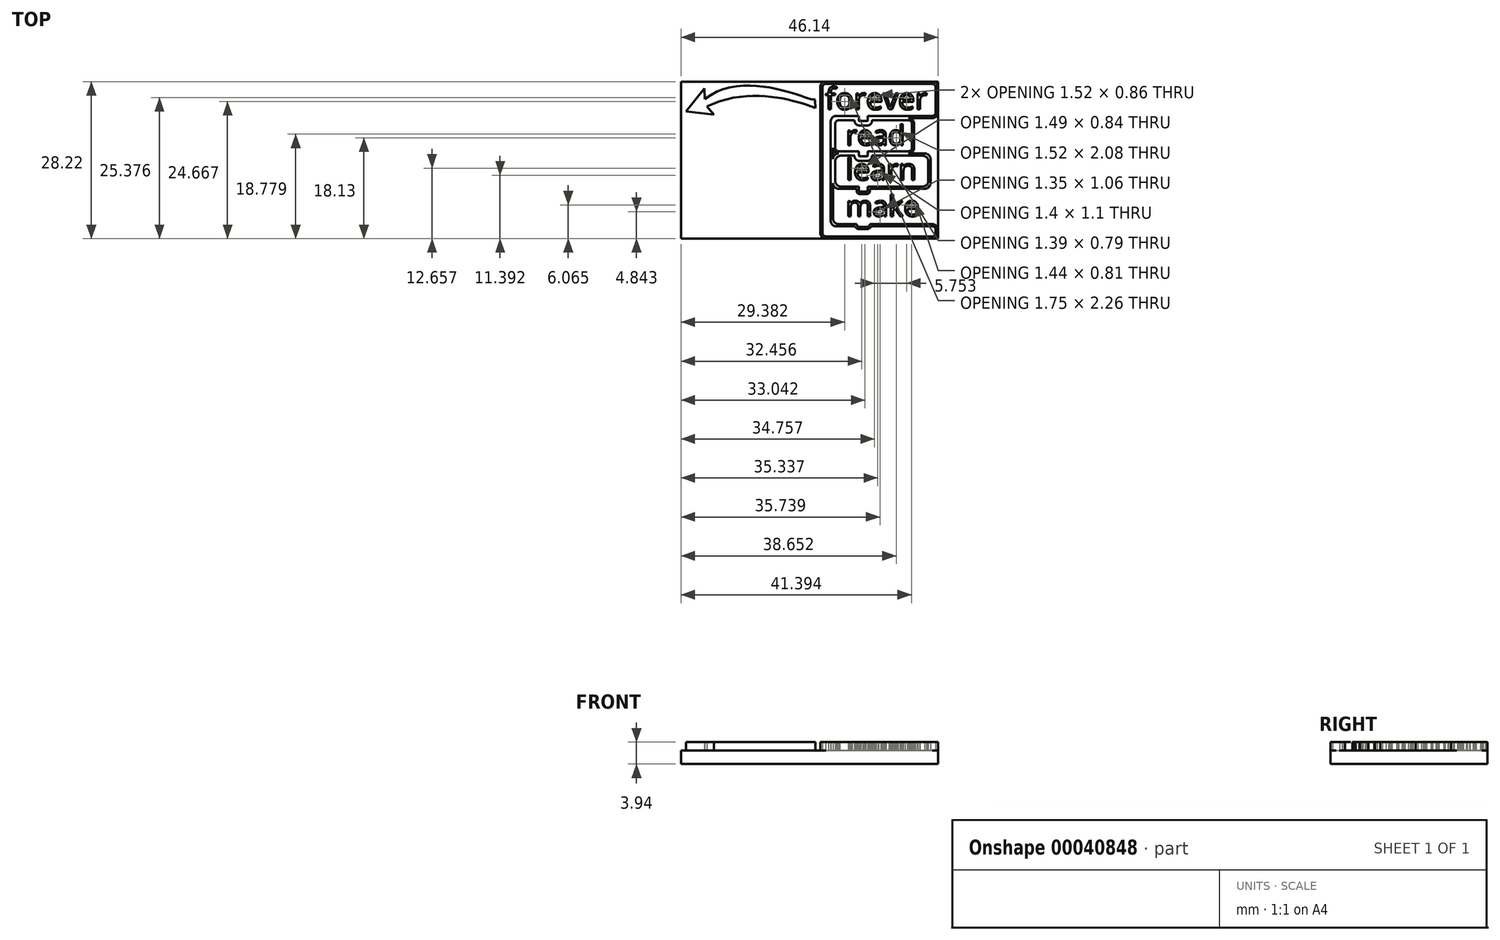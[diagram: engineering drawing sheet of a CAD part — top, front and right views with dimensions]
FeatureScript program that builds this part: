
annotation { "Feature Type Name" : "Feature", "Feature Type Description" : "" }
export const myFeature = defineFeature(function(context is Context, id is Id, definition is map)
    precondition{}
    {
        {
            var Q0;
            Q0=qCreatedBy(makeId("Top.planeOp"),FACE);
            var sketch = newSketch(context, id + "F0", { "sketchPlane" : qUnion([Q0])});
            skLineSegment(sketch, "E0", {"start": v(-1.02, 0) * mm, "end": v(-20.12, 0) * mm});
            skLineSegment(sketch, "E1", {"start": v(-21.14, -1.02) * mm, "end": v(-21.14, -27.2) * mm});
            skLineSegment(sketch, "E2", {"start": v(-20.12, -28.21) * mm, "end": v(-1.02, -28.21) * mm});
            skLineSegment(sketch, "E3", {"start": v(0, -27.2) * mm, "end": v(0, -26.62) * mm});
            skLineSegment(sketch, "E4", {"start": v(-1.02, -25.6) * mm, "end": v(-12.22, -25.6) * mm});
            skLineSegment(sketch, "E5", {"start": v(-18.86, -18.24) * mm, "end": v(-18.86, -7.57) * mm});
            skLineSegment(sketch, "E6", {"start": v(-17.84, -6.56) * mm, "end": v(-14.6, -6.56) * mm});
            skLineSegment(sketch, "E7", {"start": v(0, -5.54) * mm, "end": v(0, -1.02) * mm});
            skLineSegment(sketch, "E8.top", {"start": v(-17.84, -12.9) * mm, "end": v(-14.6, -12.9) * mm});
            skLineSegment(sketch, "E8.left", {"start": v(-18.86, -7.57) * mm, "end": v(-18.86, -11.9) * mm});
            skLineSegment(sketch, "E8.right", {"start": v(-4.27, -7.57) * mm, "end": v(-4.27, -11.9) * mm});
            skText(sketch, "E9", { "text": "read", "fontName": "OpenSans-Regular.ttf"});
            skLineSegment(sketch, "E10.top", {"start": v(-18.86, -19.26) * mm, "end": v(-14.6, -19.26) * mm});
            skLineSegment(sketch, "E10.left", {"start": v(-18.86, -13.92) * mm, "end": v(-18.86, -19.26) * mm});
            skLineSegment(sketch, "E10.right", {"start": v(-1.33, -13.92) * mm, "end": v(-1.33, -18.24) * mm});
            skText(sketch, "E11", { "text": "learn", "fontName": "OpenSans-Regular.ttf"});
            skText(sketch, "E12", { "text": "make", "fontName": "OpenSans-Regular.ttf"});
            skLineSegment(sketch, "E13.bottom", {"start": v(-17.84, -19.26) * mm, "end": v(-14.6, -19.26) * mm});
            skLineSegment(sketch, "E13.top", {"start": v(-17.86, -25.6) * mm, "end": v(-14.58, -25.6) * mm});
            skLineSegment(sketch, "E13.left", {"start": v(-18.86, -20.27) * mm, "end": v(-18.86, -24.6) * mm});
            skLineSegment(sketch, "E14", {"start": v(-14.6, -6.56) * mm, "end": v(-14.6, -6.99) * mm});
            skLineSegment(sketch, "E15", {"start": v(-14.08, -7.5) * mm, "end": v(-12.73, -7.5) * mm});
            skLineSegment(sketch, "E16", {"start": v(-12.23, -6.99) * mm, "end": v(-12.23, -6.56) * mm});
            skLineSegment(sketch, "E17", {"start": v(-14.6, -12.9) * mm, "end": v(-14.6, -13.34) * mm});
            skLineSegment(sketch, "E18", {"start": v(-14.6, -19.26) * mm, "end": v(-14.6, -19.69) * mm});
            skLineSegment(sketch, "E19", {"start": v(-14.08, -20.2) * mm, "end": v(-12.73, -20.2) * mm});
            skLineSegment(sketch, "E20", {"start": v(-12.23, -19.69) * mm, "end": v(-12.23, -19.26) * mm});
            skLineSegment(sketch, "E21", {"start": v(-14.08, -13.85) * mm, "end": v(-12.73, -13.85) * mm});
            skLineSegment(sketch, "E22", {"start": v(-12.23, -13.34) * mm, "end": v(-12.23, -12.9) * mm});
            skText(sketch, "E23", { "text": "forever", "fontName": "OpenSans-Regular.ttf"});
            skPoint(sketch, "E24.visualSharp", {"position": v(-21.14, 0) * mm});
            skArc(sketch, "E24.filletArc", {"start": v(-20.12, 0) * mm, "mid": v(-20.84, -0.3) * mm, "end": v(-21.14, -1.02) * mm});
            skPoint(sketch, "E25.visualSharp", {"position": v(0, 0) * mm});
            skArc(sketch, "E25.filletArc", {"start": v(0, -1.02) * mm, "mid": v(-0.3, -0.3) * mm, "end": v(-1.02, 0) * mm});
            skPoint(sketch, "E26.visualSharp", {"position": v(0, -6.56) * mm});
            skArc(sketch, "E26.filletArc", {"start": v(-1.02, -6.56) * mm, "mid": v(-0.3, -6.26) * mm, "end": v(0, -5.54) * mm});
            skPoint(sketch, "E27.visualSharp", {"position": v(-1.33, -12.9) * mm});
            skArc(sketch, "E27.filletArc", {"start": v(-1.33, -13.92) * mm, "mid": v(-1.63, -13.2) * mm, "end": v(-2.34, -12.9) * mm});
            skPoint(sketch, "E28.visualSharp", {"position": v(-1.33, -19.26) * mm});
            skArc(sketch, "E28.filletArc", {"start": v(-2.34, -19.26) * mm, "mid": v(-1.63, -18.96) * mm, "end": v(-1.33, -18.24) * mm});
            skPoint(sketch, "E29.visualSharp", {"position": v(0, -25.6) * mm});
            skArc(sketch, "E29.filletArc", {"start": v(0, -26.62) * mm, "mid": v(-0.3, -25.9) * mm, "end": v(-1.02, -25.6) * mm});
            skPoint(sketch, "E30.visualSharp", {"position": v(-21.14, -28.21) * mm});
            skArc(sketch, "E30.filletArc", {"start": v(-21.14, -27.2) * mm, "mid": v(-20.84, -27.92) * mm, "end": v(-20.12, -28.21) * mm});
            skPoint(sketch, "E31.visualSharp", {"position": v(-18.86, -25.6) * mm});
            skArc(sketch, "E31.filletArc", {"start": v(-18.86, -24.6) * mm, "mid": v(-18.56, -25.3) * mm, "end": v(-17.84, -25.6) * mm});
            skPoint(sketch, "E32.visualSharp", {"position": v(-18.86, -6.56) * mm});
            skArc(sketch, "E32.filletArc", {"start": v(-17.84, -6.56) * mm, "mid": v(-18.56, -6.85) * mm, "end": v(-18.86, -7.57) * mm});
            skPoint(sketch, "E33.visualSharp", {"position": v(0, -28.21) * mm});
            skArc(sketch, "E33.filletArc", {"start": v(-1.02, -28.21) * mm, "mid": v(-0.3, -27.92) * mm, "end": v(0, -27.2) * mm});
            skPoint(sketch, "E34.visualSharp", {"position": v(-4.27, -6.56) * mm});
            skArc(sketch, "E34.filletArc", {"start": v(-4.27, -7.57) * mm, "mid": v(-4.57, -6.85) * mm, "end": v(-5.28, -6.56) * mm});
            skPoint(sketch, "E35.visualSharp", {"position": v(-4.27, -12.9) * mm});
            skArc(sketch, "E35.filletArc", {"start": v(-5.28, -12.9) * mm, "mid": v(-4.57, -12.6) * mm, "end": v(-4.27, -11.9) * mm});
            skPoint(sketch, "E36.visualSharp", {"position": v(-3.03, -19.26) * mm});
            skPoint(sketch, "E37.visualSharp", {"position": v(-14.6, -7.5) * mm});
            skArc(sketch, "E37.filletArc", {"start": v(-14.6, -6.99) * mm, "mid": v(-14.44, -7.35) * mm, "end": v(-14.08, -7.5) * mm});
            skPoint(sketch, "E38.visualSharp", {"position": v(-12.23, -7.5) * mm});
            skArc(sketch, "E38.filletArc", {"start": v(-12.73, -7.5) * mm, "mid": v(-12.38, -7.35) * mm, "end": v(-12.23, -6.99) * mm});
            skPoint(sketch, "E39.visualSharp", {"position": v(-14.6, -13.85) * mm});
            skArc(sketch, "E39.filletArc", {"start": v(-14.6, -13.34) * mm, "mid": v(-14.44, -13.7) * mm, "end": v(-14.08, -13.85) * mm});
            skPoint(sketch, "E40.visualSharp", {"position": v(-12.23, -13.85) * mm});
            skArc(sketch, "E40.filletArc", {"start": v(-12.73, -13.85) * mm, "mid": v(-12.38, -13.7) * mm, "end": v(-12.23, -13.34) * mm});
            skPoint(sketch, "E41.visualSharp", {"position": v(-14.6, -20.2) * mm});
            skArc(sketch, "E41.filletArc", {"start": v(-14.6, -19.69) * mm, "mid": v(-14.44, -20.05) * mm, "end": v(-14.08, -20.2) * mm});
            skPoint(sketch, "E42.visualSharp", {"position": v(-12.23, -20.2) * mm});
            skArc(sketch, "E42.filletArc", {"start": v(-12.73, -20.2) * mm, "mid": v(-12.38, -20.05) * mm, "end": v(-12.23, -19.69) * mm});
            skLineSegment(sketch, "E43.trimOffspring", {"start": v(-12.23, -19.26) * mm, "end": v(-4.05, -19.26) * mm});
            skLineSegment(sketch, "E44.trimOffspring", {"start": v(-12.23, -12.9) * mm, "end": v(-5.28, -12.9) * mm});
            skLineSegment(sketch, "E45.trimOffspring", {"start": v(-12.23, -12.9) * mm, "end": v(-2.34, -12.9) * mm});
            skLineSegment(sketch, "E46.trimOffspring", {"start": v(-12.23, -19.26) * mm, "end": v(-2.34, -19.26) * mm});
            skLineSegment(sketch, "E47.trimOffspring", {"start": v(-12.23, -6.56) * mm, "end": v(-5.28, -6.56) * mm});
            skLineSegment(sketch, "E48.trimOffspring", {"start": v(-12.23, -6.56) * mm, "end": v(-1.02, -6.56) * mm});
            skPoint(sketch, "E49.visualSharp", {"position": v(-18.86, -12.9) * mm});
            skArc(sketch, "E49.filletArc", {"start": v(-18.86, -11.9) * mm, "mid": v(-18.56, -12.6) * mm, "end": v(-17.84, -12.9) * mm});
            skArc(sketch, "E50.filletArc", {"start": v(-18.86, -18.24) * mm, "mid": v(-18.56, -18.96) * mm, "end": v(-17.84, -19.26) * mm});
            skArc(sketch, "E51.filletArc", {"start": v(-17.84, -19.26) * mm, "mid": v(-18.56, -19.55) * mm, "end": v(-18.86, -20.27) * mm});
            skLineSegment(sketch, "E52", {"start": v(-5.28, -6.56) * mm, "end": v(-12.23, -6.56) * mm});
            skLineSegment(sketch, "E53", {"start": v(-4.05, -19.26) * mm, "end": v(-12.23, -19.26) * mm});
            skLineSegment(sketch, "E54.0", {"start": v(-17.84, -12.5) * mm, "end": v(-14.6, -12.5) * mm});
            skLineSegment(sketch, "E54.1", {"start": v(-17.84, -6.96) * mm, "end": v(-15, -6.96) * mm});
            skArc(sketch, "E54.2", {"start": v(-17.84, -6.96) * mm, "mid": v(-18.28, -7.14) * mm, "end": v(-18.46, -7.57) * mm});
            skLineSegment(sketch, "E54.3", {"start": v(-18.46, -7.57) * mm, "end": v(-18.46, -11.9) * mm});
            skArc(sketch, "E54.4", {"start": v(-18.46, -11.9) * mm, "mid": v(-18.28, -12.33) * mm, "end": v(-17.84, -12.5) * mm});
            skLineSegment(sketch, "E55.0", {"start": v(-5.28, -6.96) * mm, "end": v(-11.83, -6.96) * mm});
            skArc(sketch, "E55.1", {"start": v(-4.67, -7.57) * mm, "mid": v(-4.85, -7.14) * mm, "end": v(-5.28, -6.96) * mm});
            skLineSegment(sketch, "E55.2", {"start": v(-4.67, -7.57) * mm, "end": v(-4.67, -11.9) * mm});
            skArc(sketch, "E55.3", {"start": v(-5.28, -12.5) * mm, "mid": v(-4.85, -12.33) * mm, "end": v(-4.67, -11.9) * mm});
            skLineSegment(sketch, "E56.1", {"start": v(-12.63, -13.28) * mm, "end": v(-12.63, -12.5) * mm});
            skLineSegment(sketch, "E56.2", {"start": v(-14.02, -13.45) * mm, "end": v(-12.8, -13.45) * mm});
            skLineSegment(sketch, "E56.3", {"start": v(-14.2, -12.9) * mm, "end": v(-14.2, -13.28) * mm});
            skLineSegment(sketch, "E57", {"start": v(-14.6, -12.5) * mm, "end": v(-14.2, -12.5) * mm});
            skLineSegment(sketch, "E58", {"start": v(-14.2, -12.5) * mm, "end": v(-14.2, -12.9) * mm});
            skPoint(sketch, "E59.visualSharp", {"position": v(-14.2, -13.45) * mm});
            skArc(sketch, "E59.filletArc", {"start": v(-14.2, -13.28) * mm, "mid": v(-14.14, -13.4) * mm, "end": v(-14.02, -13.45) * mm});
            skPoint(sketch, "E60.visualSharp", {"position": v(-12.63, -13.45) * mm});
            skArc(sketch, "E60.filletArc", {"start": v(-12.8, -13.45) * mm, "mid": v(-12.68, -13.4) * mm, "end": v(-12.63, -13.28) * mm});
            skArc(sketch, "E61.0", {"start": v(-12.73, -7.9) * mm, "mid": v(-12.1, -7.63) * mm, "end": v(-11.83, -6.99) * mm});
            skLineSegment(sketch, "E61.1", {"start": v(-14.08, -7.9) * mm, "end": v(-12.73, -7.9) * mm});
            skArc(sketch, "E61.2", {"start": v(-15, -6.99) * mm, "mid": v(-14.72, -7.63) * mm, "end": v(-14.08, -7.9) * mm});
            skLineSegment(sketch, "E62", {"start": v(-15, -6.99) * mm, "end": v(-15, -6.96) * mm});
            skLineSegment(sketch, "E63", {"start": v(-11.83, -7) * mm, "end": v(-11.83, -6.96) * mm});
            skLineSegment(sketch, "E64.0", {"start": v(-1.02, -0.4) * mm, "end": v(-20.12, -0.4) * mm});
            skLineSegment(sketch, "E64.1", {"start": v(-12.23, -6.16) * mm, "end": v(-1.02, -6.16) * mm});
            skArc(sketch, "E64.2", {"start": v(-1.02, -6.16) * mm, "mid": v(-0.58, -5.98) * mm, "end": v(-0.4, -5.54) * mm});
            skLineSegment(sketch, "E64.3", {"start": v(-0.4, -5.54) * mm, "end": v(-0.4, -1.02) * mm});
            skArc(sketch, "E64.4", {"start": v(-0.4, -1.02) * mm, "mid": v(-0.58, -0.58) * mm, "end": v(-1.02, -0.4) * mm});
            skArc(sketch, "E65.1", {"start": v(-0.4, -26.62) * mm, "mid": v(-0.58, -26.19) * mm, "end": v(-1.02, -26) * mm});
            skLineSegment(sketch, "E65.2", {"start": v(-0.4, -27.2) * mm, "end": v(-0.4, -26.62) * mm});
            skArc(sketch, "E65.3", {"start": v(-1.02, -27.81) * mm, "mid": v(-0.58, -27.63) * mm, "end": v(-0.4, -27.2) * mm});
            skArc(sketch, "E65.4", {"start": v(-20.12, -0.4) * mm, "mid": v(-20.56, -0.58) * mm, "end": v(-20.74, -1.02) * mm});
            skLineSegment(sketch, "E65.5", {"start": v(-20.74, -1.02) * mm, "end": v(-20.74, -27.2) * mm});
            skArc(sketch, "E65.6", {"start": v(-20.74, -27.2) * mm, "mid": v(-20.56, -27.63) * mm, "end": v(-20.12, -27.81) * mm});
            skLineSegment(sketch, "E65.7", {"start": v(-20.12, -27.81) * mm, "end": v(-1.02, -27.81) * mm});
            skLineSegment(sketch, "E66", {"start": v(-18.86, -20.27) * mm, "end": v(-18.86, -19.26) * mm});
            skLineSegment(sketch, "E67", {"start": v(-19.26, -24.6) * mm, "end": v(-19.26, -7.17) * mm});
            skLineSegment(sketch, "E68", {"start": v(-12.23, -6.16) * mm, "end": v(-12.63, -6.16) * mm});
            skPoint(sketch, "E69.visualSharp", {"position": v(-19.26, -6.16) * mm});
            skArc(sketch, "E69.filletArc", {"start": v(-18.24, -6.16) * mm, "mid": v(-18.96, -6.45) * mm, "end": v(-19.26, -7.17) * mm});
            skLineSegment(sketch, "E70", {"start": v(-17.84, -26) * mm, "end": v(-18.24, -26) * mm});
            skLineSegment(sketch, "E71", {"start": v(-19.26, -24.6) * mm, "end": v(-19.26, -25) * mm});
            skPoint(sketch, "E72.visualSharp", {"position": v(-19.26, -26) * mm});
            skArc(sketch, "E72.filletArc", {"start": v(-19.26, -25) * mm, "mid": v(-18.96, -25.7) * mm, "end": v(-18.24, -26) * mm});
            skArc(sketch, "E73.filletArc", {"start": v(-18.86, -24.6) * mm, "mid": v(-18.56, -25.31) * mm, "end": v(-17.86, -25.6) * mm});
            skLineSegment(sketch, "E74", {"start": v(-17.84, -12.9) * mm, "end": v(-17.84, -12.9) * mm});
            skArc(sketch, "E75.filletArc", {"start": v(-17.84, -12.9) * mm, "mid": v(-18.56, -13.2) * mm, "end": v(-18.86, -13.92) * mm});
            skLineSegment(sketch, "E76", {"start": v(-18.86, -13.92) * mm, "end": v(-18.86, -18.24) * mm});
            skLineSegment(sketch, "E77", {"start": v(-18.46, -14.75) * mm, "end": v(-18.46, -17.84) * mm});
            skLineSegment(sketch, "E78", {"start": v(-18.46, -14.75) * mm, "end": v(-18.46, -14.32) * mm});
            skPoint(sketch, "E79.orphan", {"position": v(-17.84, -13.3) * mm});
            skLineSegment(sketch, "E80", {"start": v(-1.73, -15.83) * mm, "end": v(-1.73, -14.32) * mm});
            skLineSegment(sketch, "E81", {"start": v(-1.73, -15.83) * mm, "end": v(-1.73, -17.84) * mm});
            skLineSegment(sketch, "E82", {"start": v(-12.23, -18.86) * mm, "end": v(-2.74, -18.86) * mm});
            skLineSegment(sketch, "E83", {"start": v(-12.23, -18.86) * mm, "end": v(-12.63, -18.86) * mm});
            skLineSegment(sketch, "E84.0", {"start": v(-12.63, -19.69) * mm, "end": v(-12.63, -19.26) * mm});
            skLineSegment(sketch, "E84.1", {"start": v(-14.2, -19.26) * mm, "end": v(-14.2, -19.69) * mm});
            skArc(sketch, "E84.2", {"start": v(-14.2, -19.69) * mm, "mid": v(-14.16, -19.77) * mm, "end": v(-14.08, -19.8) * mm});
            skLineSegment(sketch, "E84.3", {"start": v(-14.08, -19.8) * mm, "end": v(-12.73, -19.8) * mm});
            skArc(sketch, "E84.4", {"start": v(-12.73, -19.8) * mm, "mid": v(-12.66, -19.77) * mm, "end": v(-12.63, -19.69) * mm});
            skLineSegment(sketch, "E85", {"start": v(-14.2, -19.26) * mm, "end": v(-14.2, -18.86) * mm});
            skLineSegment(sketch, "E86", {"start": v(-12.63, -19.26) * mm, "end": v(-12.63, -18.86) * mm});
            skLineSegment(sketch, "E87.trimOffspring", {"start": v(-14.2, -18.86) * mm, "end": v(-17.44, -18.86) * mm});
            skPoint(sketch, "E88.start.orphan", {"position": v(-18.86, -16.08) * mm});
            skLineSegment(sketch, "E89", {"start": v(-2.74, -13.3) * mm, "end": v(-11.83, -13.3) * mm});
            skPoint(sketch, "E90.visualSharp", {"position": v(-1.73, -13.3) * mm});
            skArc(sketch, "E90.filletArc", {"start": v(-1.73, -14.32) * mm, "mid": v(-2.03, -13.6) * mm, "end": v(-2.74, -13.3) * mm});
            skPoint(sketch, "E91.visualSharp", {"position": v(-1.73, -18.86) * mm});
            skArc(sketch, "E91.filletArc", {"start": v(-2.74, -18.86) * mm, "mid": v(-2.03, -18.56) * mm, "end": v(-1.73, -17.84) * mm});
            skPoint(sketch, "E92.visualSharp", {"position": v(-18.46, -18.86) * mm});
            skArc(sketch, "E92.filletArc", {"start": v(-18.46, -17.84) * mm, "mid": v(-18.16, -18.56) * mm, "end": v(-17.44, -18.86) * mm});
            skPoint(sketch, "E93.visualSharp", {"position": v(-18.46, -13.3) * mm});
            skArc(sketch, "E93.filletArc", {"start": v(-17.44, -13.3) * mm, "mid": v(-18.16, -13.6) * mm, "end": v(-18.46, -14.32) * mm});
            skLineSegment(sketch, "E94", {"start": v(-18.46, -22.2) * mm, "end": v(-18.46, -20.13) * mm});
            skLineSegment(sketch, "E95", {"start": v(-18.46, -22.2) * mm, "end": v(-18.46, -24.82) * mm});
            skLineSegment(sketch, "E96", {"start": v(-17.84, -19.66) * mm, "end": v(-17.84, -19.66) * mm});
            skPoint(sketch, "E97.endSnap0", {"position": v(-18.56, -25.31) * mm});
            skLineSegment(sketch, "E98", {"start": v(-2.63, -22.43) * mm, "end": v(-2.63, -24.6) * mm});
            skLineSegment(sketch, "E99", {"start": v(-2.63, -22.43) * mm, "end": v(-2.63, -20.27) * mm});
            skLineSegment(sketch, "E100", {"start": v(-17.84, -19.66) * mm, "end": v(-18, -19.66) * mm});
            skLineSegment(sketch, "E101", {"start": v(-17.84, -19.66) * mm, "end": v(-15, -19.66) * mm});
            skLineSegment(sketch, "E102", {"start": v(-3.65, -25.6) * mm, "end": v(-4.05, -25.6) * mm});
            skLineSegment(sketch, "E103", {"start": v(-4.05, -19.26) * mm, "end": v(-3.65, -19.26) * mm});
            skLineSegment(sketch, "E104", {"start": v(-11.83, -19.69) * mm, "end": v(-4.05, -19.69) * mm});
            skArc(sketch, "E105.0", {"start": v(-12.73, -20.6) * mm, "mid": v(-12.1, -20.33) * mm, "end": v(-11.83, -19.69) * mm});
            skLineSegment(sketch, "E105.1", {"start": v(-14.08, -20.6) * mm, "end": v(-12.73, -20.6) * mm});
            skArc(sketch, "E105.2", {"start": v(-15, -19.66) * mm, "mid": v(-14.74, -20.32) * mm, "end": v(-14.08, -20.6) * mm});
            skPoint(sketch, "E106.orphan", {"position": v(-11.94, -19.69) * mm});
            skLineSegment(sketch, "E107", {"start": v(-18.07, -25.19) * mm, "end": v(-14.18, -25.19) * mm});
            skLineSegment(sketch, "E108", {"start": v(-12.63, -6.16) * mm, "end": v(-12.63, -7.03) * mm});
            skLineSegment(sketch, "E109", {"start": v(-14.2, -6.16) * mm, "end": v(-14.2, -7.03) * mm});
            skLineSegment(sketch, "E110", {"start": v(-14.08, -7.1) * mm, "end": v(-14.13, -7.1) * mm});
            skLineSegment(sketch, "E111", {"start": v(-14.08, -7.1) * mm, "end": v(-12.69, -7.1) * mm});
            skPoint(sketch, "E112.visualSharp", {"position": v(-14.2, -7.1) * mm});
            skArc(sketch, "E112.filletArc", {"start": v(-14.2, -7.03) * mm, "mid": v(-14.17, -7.08) * mm, "end": v(-14.13, -7.1) * mm});
            skPoint(sketch, "E113.visualSharp", {"position": v(-12.63, -7.1) * mm});
            skArc(sketch, "E113.filletArc", {"start": v(-12.69, -7.1) * mm, "mid": v(-12.64, -7.08) * mm, "end": v(-12.63, -7.03) * mm});
            skLineSegment(sketch, "E114.trimOffspring", {"start": v(-14.2, -6.16) * mm, "end": v(-18.24, -6.16) * mm});
            skArc(sketch, "E115.0", {"start": v(-12.73, -14.25) * mm, "mid": v(-12.08, -13.97) * mm, "end": v(-11.83, -13.3) * mm});
            skLineSegment(sketch, "E115.1", {"start": v(-14.08, -14.25) * mm, "end": v(-12.73, -14.25) * mm});
            skArc(sketch, "E115.2", {"start": v(-15, -13.3) * mm, "mid": v(-14.74, -13.97) * mm, "end": v(-14.08, -14.25) * mm});
            skLineSegment(sketch, "E116.trimOffspring", {"start": v(-15, -13.3) * mm, "end": v(-17.44, -13.3) * mm});
            skLineSegment(sketch, "E117", {"start": v(-5.28, -12.5) * mm, "end": v(-12.63, -12.5) * mm});
            skPoint(sketch, "E118.visualSharp", {"position": v(-2.63, -19.26) * mm});
            skArc(sketch, "E118.filletArc", {"start": v(-2.63, -20.27) * mm, "mid": v(-2.93, -19.55) * mm, "end": v(-3.65, -19.26) * mm});
            skPoint(sketch, "E119.visualSharp", {"position": v(-3.03, -25.19) * mm});
            skArc(sketch, "E119.filletArc", {"start": v(-4.05, -25.19) * mm, "mid": v(-3.33, -24.9) * mm, "end": v(-3.03, -24.17) * mm});
            skPoint(sketch, "E120.visualSharp", {"position": v(-3.03, -19.69) * mm});
            skPoint(sketch, "E121.visualSharp", {"position": v(-2.63, -25.6) * mm});
            skArc(sketch, "E121.filletArc", {"start": v(-3.65, -25.6) * mm, "mid": v(-2.93, -25.3) * mm, "end": v(-2.63, -24.6) * mm});
            skLineSegment(sketch, "E122", {"start": v(-3.03, -24.17) * mm, "end": v(-3.03, -20.7) * mm});
            skArc(sketch, "E123.filletArc", {"start": v(-3.03, -20.7) * mm, "mid": v(-3.33, -19.99) * mm, "end": v(-4.05, -19.69) * mm});
            skArc(sketch, "E124.filletArc", {"start": v(-12.73, -26.12) * mm, "mid": v(-12.37, -25.97) * mm, "end": v(-12.22, -25.61) * mm});
            skLineSegment(sketch, "E125", {"start": v(-14.58, -25.18) * mm, "end": v(-14.58, -25.19) * mm});
            skPoint(sketch, "E126.orphan", {"position": v(-11.93, -25.61) * mm});
            skLineSegment(sketch, "E127", {"start": v(-14.08, -26.12) * mm, "end": v(-12.73, -26.12) * mm});
            skPoint(sketch, "E124.visualSharp", {"position": v(-12.22, -26.12) * mm});
            skArc(sketch, "E128.filletArc", {"start": v(-14.58, -25.61) * mm, "mid": v(-14.43, -25.97) * mm, "end": v(-14.08, -26.12) * mm});
            skLineSegment(sketch, "E129.3", {"start": v(-14.08, -25.72) * mm, "end": v(-12.73, -25.72) * mm});
            skPoint(sketch, "E128.visualSharp", {"position": v(-14.58, -26.12) * mm});
            skArc(sketch, "E129.4", {"start": v(-12.73, -25.72) * mm, "mid": v(-12.65, -25.69) * mm, "end": v(-12.62, -25.61) * mm});
            skArc(sketch, "E129.2", {"start": v(-14.18, -25.61) * mm, "mid": v(-14.15, -25.69) * mm, "end": v(-14.08, -25.72) * mm});
            skLineSegment(sketch, "E130", {"start": v(-14.18, -25.61) * mm, "end": v(-14.18, -25.19) * mm});
            skLineSegment(sketch, "E131", {"start": v(-12.62, -25.19) * mm, "end": v(-12.62, -25.61) * mm});
            skLineSegment(sketch, "E132", {"start": v(-12.22, -25.61) * mm, "end": v(-12.22, -25.6) * mm});
            skLineSegment(sketch, "E133.trimOffspring", {"start": v(-12.62, -25.19) * mm, "end": v(-4.05, -25.19) * mm});
            skLineSegment(sketch, "E134.trimOffspring", {"start": v(-14.58, -25.6) * mm, "end": v(-17.84, -25.6) * mm});
            skLineSegment(sketch, "E135.trimOffspring", {"start": v(-11.82, -25.6) * mm, "end": v(-4.05, -25.6) * mm});
            skLineSegment(sketch, "E136.trimOffspring", {"start": v(-14.58, -25.6) * mm, "end": v(-14.58, -25.61) * mm});
            skLineSegment(sketch, "E137", {"start": v(-14.58, -25.6) * mm, "end": v(-14.98, -25.6) * mm});
            skLineSegment(sketch, "E138", {"start": v(-12.22, -25.6) * mm, "end": v(-11.82, -25.6) * mm});
            skLineSegment(sketch, "E139", {"start": v(-11.82, -25.5) * mm, "end": v(-11.82, -25.6) * mm});
            skPoint(sketch, "E140.visualSharp", {"position": v(-11.82, -26.52) * mm});
            skArc(sketch, "E140.filletArc", {"start": v(-12.84, -26.52) * mm, "mid": v(-12.32, -26.38) * mm, "end": v(-11.95, -26) * mm});
            skArc(sketch, "E141", {"start": v(-14.9, -26) * mm, "mid": v(-14.6, -26.36) * mm, "end": v(-14.17, -26.52) * mm});
            skLineSegment(sketch, "E142", {"start": v(-14.17, -26.52) * mm, "end": v(-12.84, -26.52) * mm});
            skLineSegment(sketch, "E143.trimOffspring", {"start": v(-14.9, -26) * mm, "end": v(-17.84, -26) * mm});
            skLineSegment(sketch, "E144", {"start": v(-1.02, -26) * mm, "end": v(-11.95, -26) * mm});
            skArc(sketch, "E145.trimOffspring", {"start": v(-11.82, -25.6) * mm, "mid": v(-11.82, -25.56) * mm, "end": v(-11.82, -25.5) * mm});
            skPoint(sketch, "E146.visualSharp", {"position": v(-18.46, -25.19) * mm});
            skArc(sketch, "E147", {"start": v(-18.46, -24.76) * mm, "mid": v(-18.36, -25.06) * mm, "end": v(-18.07, -25.19) * mm});
            skArc(sketch, "E148", {"start": v(-18, -19.66) * mm, "mid": v(-18.32, -19.8) * mm, "end": v(-18.46, -20.13) * mm});
            const initialGuessF0  = {"E9": [-0.01653, -0.01142, 1, 0, 0.00358], "E11": [-0.01653, -0.01768, 1, 0, 0.00383], "E12": [-0.01653, -0.0242, 1, 0, 0.0037], "E23": [-0.02023, -0.005, 1, 0, 0.0039]};
            skSetInitialGuess(sketch, initialGuessF0);
            skSolve(sketch);
        }
        {
            var Q0;
            Q0=makeQuery(id+"F0.imprint","IMPRINT",FACE,{"disambiguationData":[TD([[makeQuery(id+"F0.imprint","IMPRINT",EDGE,{"derivedFrom":sQuery(id+"F0.wireOp",EDGE,"E23.sketch_text.stroke-0")}),-1.0]])]});
            var Q1;
            Q1=makeQuery(id+"F0.imprint","IMPRINT",FACE,{"disambiguationData":[TD([[makeQuery(id+"F0.imprint","IMPRINT",EDGE,{"derivedFrom":sQuery(id+"F0.wireOp",EDGE,"E23.sketch_text.stroke-17")}),-1.0]])]});
            var Q2;
            Q2=makeQuery(id+"F0.imprint","IMPRINT",FACE,{"disambiguationData":[TD([[makeQuery(id+"F0.imprint","IMPRINT",EDGE,{"derivedFrom":sQuery(id+"F0.wireOp",EDGE,"E23.sketch_text.stroke-34")}),-1.0]])]});
            var Q3;
            Q3=makeQuery(id+"F0.imprint","IMPRINT",FACE,{"disambiguationData":[TD([[makeQuery(id+"F0.imprint","IMPRINT",EDGE,{"derivedFrom":sQuery(id+"F0.wireOp",EDGE,"E23.sketch_text.stroke-47")}),-1.0]])]});
            var Q4;
            Q4=makeQuery(id+"F0.imprint","IMPRINT",FACE,{"disambiguationData":[TD([[makeQuery(id+"F0.imprint","IMPRINT",EDGE,{"derivedFrom":sQuery(id+"F0.wireOp",EDGE,"E23.sketch_text.stroke-66")}),-1.0]])]});
            var Q5;
            Q5=makeQuery(id+"F0.imprint","IMPRINT",FACE,{"disambiguationData":[TD([[makeQuery(id+"F0.imprint","IMPRINT",EDGE,{"derivedFrom":sQuery(id+"F0.wireOp",EDGE,"E23.sketch_text.stroke-76")}),-1.0]])]});
            var Q6;
            Q6=makeQuery(id+"F0.imprint","IMPRINT",FACE,{"disambiguationData":[TD([[makeQuery(id+"F0.imprint","IMPRINT",EDGE,{"derivedFrom":sQuery(id+"F0.wireOp",EDGE,"E23.sketch_text.stroke-95")}),-1.0]])]});
            var Q7;
            Q7=makeQuery(id+"F0.imprint","IMPRINT",FACE,{"disambiguationData":[TD([[makeQuery(id+"F0.imprint","IMPRINT",EDGE,{"derivedFrom":sQuery(id+"F0.wireOp",EDGE,"E9.sketch_text.stroke-0")}),-1.0]])]});
            var Q8;
            Q8=makeQuery(id+"F0.imprint","IMPRINT",FACE,{"disambiguationData":[TD([[makeQuery(id+"F0.imprint","IMPRINT",EDGE,{"derivedFrom":sQuery(id+"F0.wireOp",EDGE,"E9.sketch_text.stroke-13")}),-1.0]])]});
            var Q9;
            Q9=makeQuery(id+"F0.imprint","IMPRINT",FACE,{"disambiguationData":[TD([[makeQuery(id+"F0.imprint","IMPRINT",EDGE,{"derivedFrom":sQuery(id+"F0.wireOp",EDGE,"E9.sketch_text.stroke-32")}),-1.0]])]});
            var Q10;
            Q10=makeQuery(id+"F0.imprint","IMPRINT",FACE,{"disambiguationData":[TD([[makeQuery(id+"F0.imprint","IMPRINT",EDGE,{"derivedFrom":sQuery(id+"F0.wireOp",EDGE,"E11.sketch_text.stroke-0")}),-1.0]])]});
            extrude(context, id + "F1", {"entities" : qUnion([Q0, Q1, Q2, Q3, Q4, Q5, Q6, Q7, Q8, Q9, Q10]), "depth" : 1.5 * mm});
        }
        {
            var Q0;
            Q0=makeQuery(id+"F0.imprint","IMPRINT",FACE,{"disambiguationData":[TD([[makeQuery(id+"F0.imprint","IMPRINT",EDGE,{"derivedFrom":sQuery(id+"F0.wireOp",EDGE,"E12.sketch_text.stroke-0")}),-1.0]])]});
            var Q1;
            Q1=makeQuery(id+"F0.imprint","IMPRINT",FACE,{"disambiguationData":[TD([[makeQuery(id+"F0.imprint","IMPRINT",EDGE,{"derivedFrom":sQuery(id+"F0.wireOp",EDGE,"E12.sketch_text.stroke-28")}),-1.0]])]});
            var Q2;
            Q2=makeQuery(id+"F0.imprint","IMPRINT",FACE,{"disambiguationData":[TD([[makeQuery(id+"F0.imprint","IMPRINT",EDGE,{"derivedFrom":sQuery(id+"F0.wireOp",EDGE,"E12.sketch_text.stroke-55")}),-1.0]])]});
            var Q3;
            Q3=makeQuery(id+"F0.imprint","IMPRINT",FACE,{"disambiguationData":[TD([[makeQuery(id+"F0.imprint","IMPRINT",EDGE,{"derivedFrom":sQuery(id+"F0.wireOp",EDGE,"E12.sketch_text.stroke-70")}),-1.0]])]});
            extrude(context, id + "F2", {"entities" : qUnion([Q0, Q1, Q2, Q3]), "depth" : 1.5 * mm});
        }
        {
            var Q0;
            Q0=makeQuery(id+"F0.imprint","IMPRINT",FACE,{"disambiguationData":[TD([[makeQuery(id+"F0.imprint","IMPRINT",EDGE,{"derivedFrom":sQuery(id+"F0.wireOp",EDGE,"E11.sketch_text.stroke-4")}),-1.0]])]});
            var Q1;
            Q1=makeQuery(id+"F0.imprint","IMPRINT",FACE,{"disambiguationData":[TD([[makeQuery(id+"F0.imprint","IMPRINT",EDGE,{"derivedFrom":sQuery(id+"F0.wireOp",EDGE,"E11.sketch_text.stroke-23")}),-1.0]])]});
            var Q2;
            Q2=makeQuery(id+"F0.imprint","IMPRINT",FACE,{"disambiguationData":[TD([[makeQuery(id+"F0.imprint","IMPRINT",EDGE,{"derivedFrom":sQuery(id+"F0.wireOp",EDGE,"E11.sketch_text.stroke-50")}),-1.0]])]});
            var Q3;
            Q3=makeQuery(id+"F0.imprint","IMPRINT",FACE,{"disambiguationData":[TD([[makeQuery(id+"F0.imprint","IMPRINT",EDGE,{"derivedFrom":sQuery(id+"F0.wireOp",EDGE,"E11.sketch_text.stroke-63")}),-1.0]])]});
            extrude(context, id + "F3", {"entities" : qUnion([Q0, Q1, Q2, Q3]), "depth" : 1.5 * mm});
        }
        {
            var Q0;
            Q0=makeQuery(id+"F0.imprint","IMPRINT",FACE,{"disambiguationData":[TD([[makeQuery(id+"F0.imprint","IMPRINT",EDGE,{"derivedFrom":sQuery(id+"F0.wireOp",EDGE,"E9.sketch_text.stroke-59")}),-1.0]])]});
            var Q1;
            Q1=makeQuery(id+"F0.imprint","IMPRINT",FACE,{"disambiguationData":[TD([[makeQuery(id+"F0.imprint","IMPRINT",EDGE,{"derivedFrom":sQuery(id+"F0.wireOp",EDGE,"E0")}),1.0]])]});
            var Q2;
            Q2=makeQuery(id+"F0.imprint","IMPRINT",FACE,{"disambiguationData":[TD([[makeQuery(id+"F0.imprint","IMPRINT",EDGE,{"derivedFrom":sQuery(id+"F0.wireOp",EDGE,"E6")}),-1.0]])]});
            var Q3;
            Q3=makeQuery(id+"F0.imprint","IMPRINT",FACE,{"disambiguationData":[TD([[makeQuery(id+"F0.imprint","IMPRINT",EDGE,{"derivedFrom":sQuery(id+"F0.wireOp",EDGE,"E8.top")}),-1.0]])]});
            var Q4;
            Q4=makeQuery(id+"F0.imprint","IMPRINT",FACE,{"disambiguationData":[TD([[makeQuery(id+"F0.imprint","IMPRINT",EDGE,{"derivedFrom":sQuery(id+"F0.wireOp",EDGE,"E13.bottom")}),-1.0]])]});
            extrude(context, id + "F4", {"entities" : qUnion([Q0, Q1, Q2, Q3, Q4]), "depth" : 1.5 * mm});
        }
        {
            var Q0;
            Q0=qCreatedBy(makeId("Right.planeOp"),FACE);
            var sketch = newSketch(context, id + "F5", { "sketchPlane" : qUnion([Q0])});
            skLineSegment(sketch, "E149", {"start": v(0, 0) * mm, "end": v(0, -2.44) * mm});
            skLineSegment(sketch, "E150", {"start": v(0, -2.44) * mm, "end": v(-28.22, -2.44) * mm});
            skLineSegment(sketch, "E151", {"start": v(0, 0) * mm, "end": v(-28.22, 0) * mm});
            skLineSegment(sketch, "E152", {"start": v(-28.22, 0) * mm, "end": v(-28.22, -2.44) * mm});
            skSolve(sketch);
        }
        {
            var Q0;
            Q0 = qSketchRegion(id + "F5", true);
            var Q1;
            Q1=makeQuery(id+"F5.imprint","IMPRINT",FACE,{"disambiguationData":[TD([[makeQuery(id+"F5.imprint","IMPRINT",EDGE,{"derivedFrom":sQuery(id+"F5.wireOp",EDGE,"E149")}),-1.0]])]});
            var Q2;
            Q2=makeQuery(id+"F4.opExtrude","SWEPT_FACE",FACE,{"disambiguationData":[OSD([sQuery(id+"F0.wireOp",EDGE,"E1")])]});
            extrude(context, id + "F6", {"entities" : qUnion([Q0, Q1]), "endBound" : BoundingType.UP_TO_SURFACE, "oppositeDirection" : true, "endBoundEntityFace" : qUnion([Q2]), "depth" : 25 * mm});
        }
        {
            var Q0;
            Q0=makeQuery(id+"F6.opExtrude","CAP_FACE",FACE,{"disambiguationData":[OSD([sQuery(id+"F5.wireOp",EDGE,"E149"),sQuery(id+"F5.wireOp",EDGE,"E150"),sQuery(id+"F5.wireOp",EDGE,"E151"),sQuery(id+"F5.wireOp",EDGE,"E152")])],"isStart":false});
            extrude(context, id + "F7", {"entities" : qUnion([Q0]), "operationType" : NewBodyOperationType.ADD, "depth" : 25 * mm});
        }
        {
            var Q0;
            {var subQ0=sQuery(id+"F5.wireOp",EDGE,"E151");Q0=makeQuery(id+"F7.boolean.opBoolean","MERGE",FACE,{"derivedFrom":[makeQuery(id+"F6.opExtrude","SWEPT_FACE",FACE,{"disambiguationData":[OSD([subQ0])]}),makeQuery(id+"F7.opExtrude","SWEPT_FACE",FACE,{"disambiguationData":[OSD([subQ0])]})]});}
            var sketch = newSketch(context, id + "F8", { "sketchPlane" : qUnion([Q0])});
            skFitSpline(sketch, "E153", {"points": [v(-41.89, -3.14) * mm, v(-22.8, -3.14) * mm, v(-22.08, -3.23) * mm], "startDerivative": vector(23.92, 18.67) * mm, "endDerivative": vector(2.94, -0.6) * mm});
            skFitSpline(sketch, "E154", {"points": [v(-41.48, -4.47) * mm, v(-22.01, -4.76) * mm, v(-22.1, -4.7) * mm], "startDerivative": vector(28.75, 14.4) * mm, "endDerivative": vector(-2.15, 0.72) * mm});
            skLineSegment(sketch, "E155", {"start": v(-41.89, -3.14) * mm, "end": v(-41.95, -1.24) * mm});
            skLineSegment(sketch, "E156", {"start": v(-41.95, -1.24) * mm, "end": v(-45.23, -5.37) * mm});
            skLineSegment(sketch, "E157", {"start": v(-45.23, -5.37) * mm, "end": v(-40.24, -5.94) * mm});
            skLineSegment(sketch, "E158", {"start": v(-40.24, -5.94) * mm, "end": v(-41.48, -4.47) * mm});
            skLineSegment(sketch, "E159", {"start": v(-22.01, -4.76) * mm, "end": v(-22.08, -3.23) * mm});
            skSolve(sketch);
        }
        {
            var Q0;
            {var subQ3=sQuery(id+"F8.wireOp",EDGE,"E153");Q0=makeQuery(id+"F8.imprint","IMPRINT",FACE,{"disambiguationData":[TD([[makeQuery(id+"F8.imprint","IMPRINT",EDGE,{"derivedFrom":subQ3}),-1.0]])]});}
            extrude(context, id + "F9", {"entities" : qUnion([Q0]), "operationType" : NewBodyOperationType.ADD, "depth" : 1.5 * mm});
        }
    });
